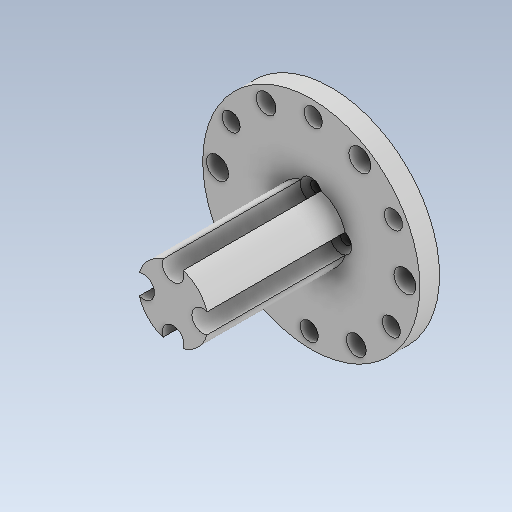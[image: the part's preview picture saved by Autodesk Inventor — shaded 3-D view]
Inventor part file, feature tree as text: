
AUTODESK INVENTOR PART (.ipt)
format: ipt  version: 2020 (Build 240168000, 168)  size: 275,968 bytes
history: native  units: mm
features: reference x12, other x5, extrude x4, sketch x4, fillet x1, hole x1
ambient origin geometry x8: Origin, YZ Plane, XZ Plane, XY Plane, X Axis, Y Axis, Z Axis, Center Point
bodies: Solid1 (feature_tree)
feature tree (27):
  extrude  "Extrusion1"  Depth=35.0mm TaperAngle=0.0deg
  extrude  "Extrusion2"  Depth=5.0mm TaperAngle=0.0deg
  fillet  "Fillet1"  Radius=5.0mm
  extrude  "Extrusion3"  Depth=10.0mm
  hole  "Hole2"  [1 undecoded]
  extrude  "Extrusion4"  [1 undecoded]
  sketch  "Sketch1"  dims[d0=35.0mm d1=2.0mm d2=0.0mm]
  sketch  "Sketch2"  dims[d3=55.0mm d4=5.0mm d5=0.0mm d6=5.0mm]
  sketch  "Sketch3"  dims[d7=10.0mm d8=0.0mm d9=17.9mm]
  reference  "Reference3"
  reference  "Reference4"
  reference  "Reference5"
  reference  "Reference6"
  reference  "Reference7"
  reference  "Reference8"
  reference  "Reference9"
  reference  "Reference10"
  reference  "Reference11"
  reference  "Reference12"
  reference  "Reference13"
  reference  "Reference14"
  sketch  "Sketch5"  dims[d12=15.0mm d20=2.9mm d21=6.0mm d22=5.5mm d23=2.0mm d24=90.0deg d25=20.0mm d26=0.0mm d27=35.0mm d28=0.0mm]
  other  "<userpath>\Desktop\KangKangBalancing\KangKang.iam"
  other  "KangKang.iam"
  other  "100mm-Plastic-Omni-Wheel:1"
  other  "A1_ASM_20"
  other  "F2_19"
note: 2 required parameter values undecoded (feature->parameter linkage not recoverable at this tier; creation-order binding heuristic only, values carry confidence <= 0.55)
